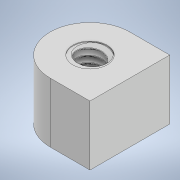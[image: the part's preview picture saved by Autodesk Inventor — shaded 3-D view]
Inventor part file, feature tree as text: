
AUTODESK INVENTOR PART (.ipt)
format: ipt  version: 2022.2 (Build 262287000, 287)  size: 663,040 bytes
history: native  units: mm
features: sketch x3, revolve x1, helix x1, extrude x1
ambient origin geometry x8: Origin, YZ Plane, XZ Plane, XY Plane, X Axis, Y Axis, Z Axis, Center Point
bodies: Solid2 (feature_tree)
feature tree (6):
  revolve  "Revolution1"  [1 undecoded]
  helix  "Coil1"  [1 undecoded]
  extrude  "Extrusion2"  Depth=2.5mm
  sketch  "Sketch2"  dims[d10=9.599311mm d11=0.064033mm d12=0.064033mm d15=0.4mm d17=9.599311mm]
  sketch  "Sketch3"  dims[d19=0.0mm]
  sketch  "Sketch5"  dims[d20=0.4004mm d21=4.5mm d22=10.0mm d23=0.0mm d24=0.0mm d25=0.0mm d26=0.0mm d27=0.0mm d30=2.5mm d31=2.5mm d32=5.0mm d33=2.5mm d34=3.75mm d35=0.0mm]
note: 2 required parameter values undecoded (feature->parameter linkage not recoverable at this tier; creation-order binding heuristic only, values carry confidence <= 0.55)